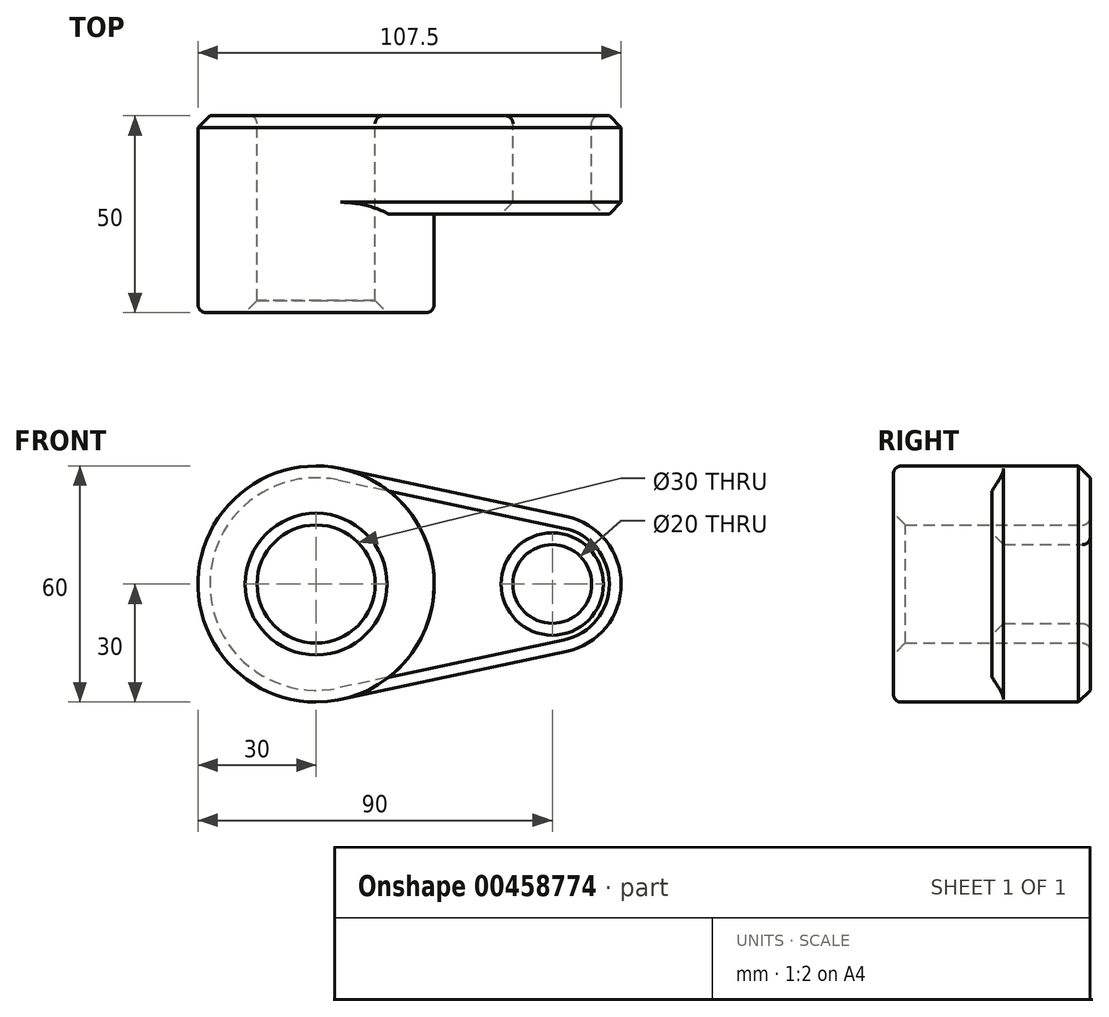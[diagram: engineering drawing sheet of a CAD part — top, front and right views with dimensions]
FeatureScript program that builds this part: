
annotation { "Feature Type Name" : "Feature", "Feature Type Description" : "" }
export const myFeature = defineFeature(function(context is Context, id is Id, definition is map)
    precondition{}
    {
        {
            var Q0;
            Q0=qCreatedBy(makeId("Front.planeOp"),FACE);
            var sketch = newSketch(context, id + "F0", { "sketchPlane" : qUnion([Q0])});
            skCircle(sketch, "E0", {"center": v(0, 0) * mm, "radius": 30 * mm});
            skCircle(sketch, "E1", {"center": v(60, 0) * mm, "radius": 17.5 * mm});
            skLineSegment(sketch, "E2", {"start": v(6.25, 29.34) * mm, "end": v(63.65, 17.12) * mm});
            skLineSegment(sketch, "E3", {"start": v(6.25, -29.34) * mm, "end": v(63.65, -17.12) * mm});
            skCircle(sketch, "E4", {"center": v(0, 0) * mm, "radius": 15 * mm});
            skCircle(sketch, "E5", {"center": v(60, 0) * mm, "radius": 10 * mm});
            skSolve(sketch);
        }
        {
            var Q0;
            Q0 = qSketchRegion(id + "F0", true);
            extrude(context, id + "F1", {"entities" : qUnion([Q0]), "depth" : 25 * mm});
        }
        {
            var Q0;
            Q0=makeQuery(id+"F0.imprint","IMPRINT",FACE,{"disambiguationData":[TD([[makeQuery(id+"F0.imprint","IMPRINT",EDGE,{"derivedFrom":sQuery(id+"F0.wireOp",EDGE,"E4")}),-1.0]])]});
            extrude(context, id + "F2", {"entities" : qUnion([Q0]), "operationType" : NewBodyOperationType.ADD, "depth" : 50 * mm});
        }
        {
            var Q0;
            Q0=makeQuery(id+"F2.opExtrude","CAP_EDGE",EDGE,{"disambiguationData":[OSD([sQuery(id+"F0.wireOp",EDGE,"E0")])],"isStart":false});
            fillet(context, id + "F3", {"entities" : qUnion([Q0]), "radius" : 2 * mm, "tangentPropagation" : true, "allowEdgeOverflow" : false});
        }
        {
            var Q0;
            Q0=makeQuery(id+"F2.opExtrude","CAP_EDGE",EDGE,{"disambiguationData":[OSD([sQuery(id+"F0.wireOp",EDGE,"E4")])],"isStart":false});
            chamfer(context, id + "F4", {"entities" : qUnion([Q0]), "width" : 3 * mm, "tangentPropagation" : true});
        }
        {
            var Q0;
            Q0=makeQuery(id+"F1.opExtrude","CAP_EDGE",EDGE,{"disambiguationData":[OSD([sQuery(id+"F0.wireOp",EDGE,"E5")])],"isStart":false});
            var Q1;
            Q1=makeQuery(id+"F1.opExtrude","CAP_EDGE",EDGE,{"disambiguationData":[OSD([sQuery(id+"F0.wireOp",EDGE,"E1")])],"isStart":false});
            var Q2;
            Q2=makeQuery(id+"F1.opExtrude","CAP_EDGE",EDGE,{"disambiguationData":[OSD([sQuery(id+"F0.wireOp",EDGE,"E2")])],"isStart":false});
            var Q3;
            Q3=makeQuery(id+"F1.opExtrude","CAP_EDGE",EDGE,{"disambiguationData":[OSD([sQuery(id+"F0.wireOp",EDGE,"E2")])],"isStart":true});
            var Q4;
            Q4=makeQuery(id+"F1.opExtrude","CAP_EDGE",EDGE,{"disambiguationData":[OSD([sQuery(id+"F0.wireOp",EDGE,"E1")])],"isStart":true});
            var Q5;
            Q5=makeQuery(id+"F1.opExtrude","CAP_EDGE",EDGE,{"disambiguationData":[OSD([sQuery(id+"F0.wireOp",EDGE,"E3")])],"isStart":true});
            var Q6;
            Q6=makeQuery(id+"F1.opExtrude","CAP_EDGE",EDGE,{"disambiguationData":[OSD([sQuery(id+"F0.wireOp",EDGE,"E0")])],"isStart":true});
            chamfer(context, id + "F5", {"entities" : qUnion([Q0, Q1, Q2, Q3, Q4, Q5, Q6]), "width" : 3 * mm, "tangentPropagation" : true});
        }
        {
            var Q0;
            Q0=makeQuery(id+"F1.opExtrude","CAP_EDGE",EDGE,{"disambiguationData":[OSD([sQuery(id+"F0.wireOp",EDGE,"E4")])],"isStart":true});
            var Q1;
            Q1=makeQuery(id+"F1.opExtrude","CAP_EDGE",EDGE,{"disambiguationData":[OSD([sQuery(id+"F0.wireOp",EDGE,"E5")])],"isStart":true});
            fillet(context, id + "F6", {"entities" : qUnion([Q0, Q1]), "radius" : 2 * mm, "tangentPropagation" : true, "allowEdgeOverflow" : false});
        }
    });
